# Revit family: Shower_Diverter-American_Standard-Serin-T064.430
name_source: partatom
category: Plumbing Fixtures
revit_build: Autodesk Revit 2014 (Build: 20130308_1515(x64)
units: mm (PartAtom-declared; Revit-internal decimal feet)

## types (1)
- T064.430
    ADA Compliant = Yes
    Assembly Code = D2010710
    CW Connection = Yes
    CWFU = 3
    Cold Water Connection Diameter = 1/2"
    Cold Water Connection Radius = 1/4"
    Default Elevation = 46"
    Description = Serin Diverter Valve Trim Kit
    HW Connection = Yes
    HWFU = 3
    Height = 2 1/8"
    Hot Water Connection Diameter = 1/2"
    Hot Water Connection Radius = 1/4"
    Installation Type = Wall Mounted
    Length = 2 1/8"
    Manufacturer = American Standard
    Material = <By Category>
    Model = T064.430
    Price = Prices may vary. Please consult Manufacturer Representative for most up-to-date price list.
    Product Documentation Link = https://www.americanstandard-us.com
    Product Page URL = https://www.americanstandard-us.com
    URL = http://www.americanstandard-us.com
    Vent Connection = No
    WFU = 4
    Warranty Information = 1 Year Limited
    Waste Connection = No
    Width = 2 5/8"

## geometry (parser evidence)
native form markers: Sweep x3
no freeform markers — native parametric forms only
